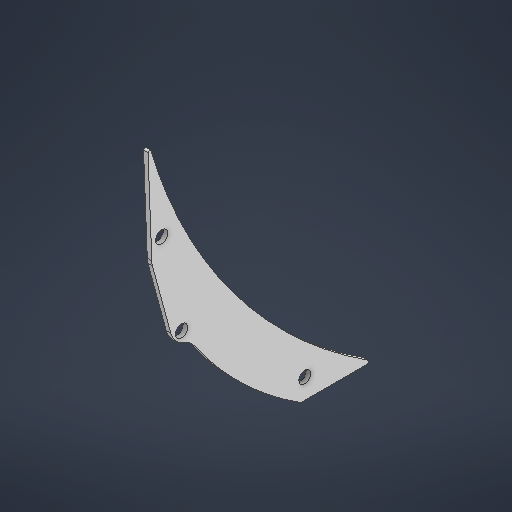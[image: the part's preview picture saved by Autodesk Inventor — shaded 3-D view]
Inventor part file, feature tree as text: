
AUTODESK INVENTOR PART (.ipt)
format: ipt  version: 2025.2 (Build 292293000, 293)  size: 204,288 bytes
history: native  units: in
note: dims shown in document units (in); Inventor stores cm internally (conversion verified against a paired STEP export)
features: extrude x1, sketch x1
ambient origin geometry x8: Origin, YZ Plane, XZ Plane, XY Plane, X Axis, Y Axis, Z Axis, Center Point
bodies: Solid1 (feature_tree)
feature tree (2):
  extrude  "Extrusion1"  Depth=0.0625in
  sketch  "Sketch1"  dims[d1=0.165in d4=1.0in d5=0.025in d6=0.0625in d7=0.0in]
